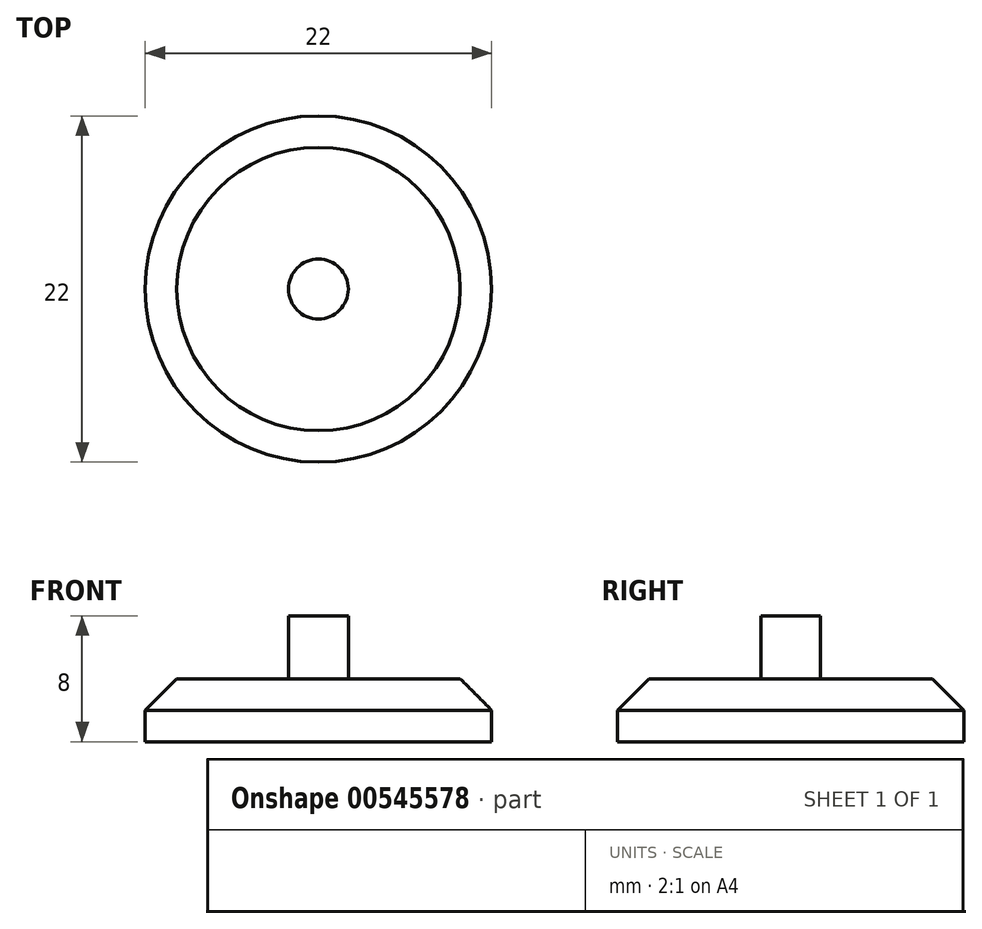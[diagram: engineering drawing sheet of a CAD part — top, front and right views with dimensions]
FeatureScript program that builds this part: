
annotation { "Feature Type Name" : "Feature", "Feature Type Description" : "" }
export const myFeature = defineFeature(function(context is Context, id is Id, definition is map)
    precondition{}
    {
        {
            var Q0;
            Q0=qCreatedBy(makeId("Top.planeOp"),FACE);
            var sketch = newSketch(context, id + "F0", { "sketchPlane" : qUnion([Q0])});
            skCircle(sketch, "E0", {"center": v(0, 0) * mm, "radius": 11 * mm});
            skSolve(sketch);
        }
        {
            var Q0;
            Q0 = qSketchRegion(id + "F0", true);
            extrude(context, id + "F1", {"entities" : qUnion([Q0]), "oppositeDirection" : true, "depth" : 4 * mm, "offsetDistance" : 25 * mm});
        }
        {
            var Q0;
            Q0=makeQuery(id+"F1.opExtrude","CAP_FACE",FACE,{"disambiguationData":[OSD([sQuery(id+"F0.wireOp",EDGE,"E0")])],"isStart":true});
            var sketch = newSketch(context, id + "F2", { "sketchPlane" : qUnion([Q0])});
            skCircle(sketch, "E1", {"center": v(0, 0) * mm, "radius": 1.9 * mm});
            skSolve(sketch);
        }
        {
            var Q0;
            Q0=makeQuery(id+"F2.imprint","IMPRINT",FACE,{"disambiguationData":[TD([[makeQuery(id+"F2.imprint","IMPRINT",EDGE,{"derivedFrom":sQuery(id+"F2.wireOp",EDGE,"E1")}),1.0]])]});
            extrude(context, id + "F3", {"entities" : qUnion([Q0]), "operationType" : NewBodyOperationType.ADD, "depth" : 4 * mm, "offsetDistance" : 25 * mm});
        }
        {
            var Q0;
            Q0=makeQuery(id+"F1.opExtrude","CAP_EDGE",EDGE,{"disambiguationData":[OSD([sQuery(id+"F0.wireOp",EDGE,"E0")])],"isStart":true});
            chamfer(context, id + "F4", {"entities" : qUnion([Q0]), "width" : 2 * mm, "tangentPropagation" : true});
        }
    });
